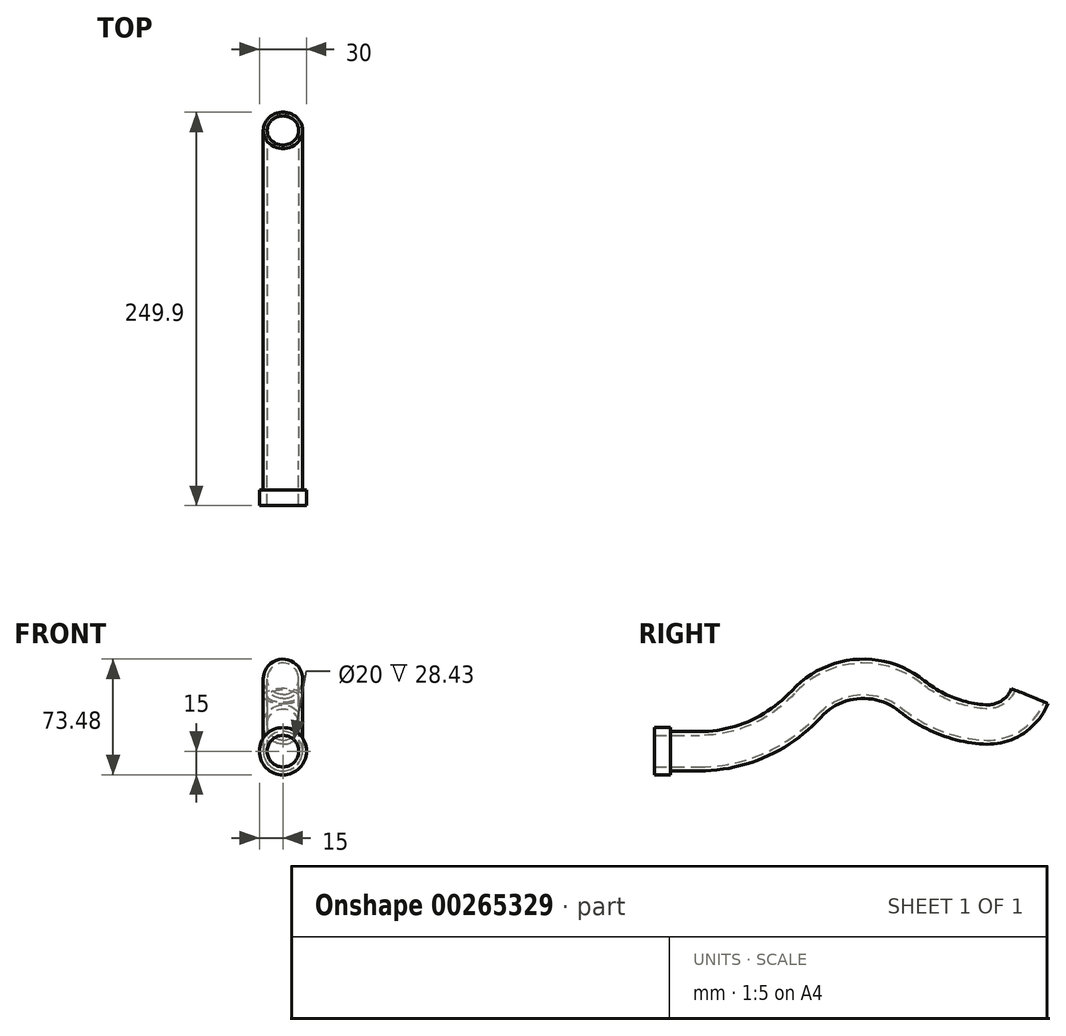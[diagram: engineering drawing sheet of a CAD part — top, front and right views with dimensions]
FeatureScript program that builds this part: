
annotation { "Feature Type Name" : "Feature", "Feature Type Description" : "" }
export const myFeature = defineFeature(function(context is Context, id is Id, definition is map)
    precondition{}
    {
        {
            var Q0;
            Q0=qCreatedBy(makeId("Front.planeOp"),FACE);
            var sketch = newSketch(context, id + "F0", { "sketchPlane" : qUnion([Q0])});
            skCircle(sketch, "E0", {"center": v(0, 0) * mm, "radius": 12.5 * mm});
            skCircle(sketch, "E1", {"center": v(0, 0) * mm, "radius": 10 * mm});
            skSolve(sketch);
        }
        {
            var Q0;
            Q0=qCreatedBy(makeId("Right.planeOp"),FACE);
            var sketch = newSketch(context, id + "F1", { "sketchPlane" : qUnion([Q0])});
            skLineSegment(sketch, "E2", {"start": v(0, 0) * mm, "end": v(28.43, 0) * mm});
            skArc(sketch, "E3", {"start": v(28.43, 0) * mm, "mid": v(65.58, 7.83) * mm, "end": v(96.4, 30) * mm});
            skArc(sketch, "E4", {"start": v(96.4, 30) * mm, "mid": v(128.96, 45.84) * mm, "end": v(163.51, 35) * mm});
            skArc(sketch, "E5", {"start": v(163.51, 35) * mm, "mid": v(185.2, 22.38) * mm, "end": v(209.72, 17) * mm});
            skArc(sketch, "E6", {"start": v(209.72, 17) * mm, "mid": v(226.91, 21.4) * mm, "end": v(238.32, 35) * mm});
            skSolve(sketch);
        }
        {
            var Q0;
            Q0 = qSketchRegion(id + "F0", true);
            var Q1;
            Q1=sQuery(id+"F1.wireOp",EDGE,"E2");
            var Q2;
            Q2=sQuery(id+"F1.wireOp",EDGE,"E3");
            var Q3;
            Q3=sQuery(id+"F1.wireOp",EDGE,"E4");
            var Q4;
            Q4=sQuery(id+"F1.wireOp",EDGE,"E5");
            var Q5;
            Q5=sQuery(id+"F1.wireOp",EDGE,"E6");
            sweep(context, id + "F2", {"profiles" : qUnion([Q0]), "path" : qUnion([Q1, Q2, Q3, Q4, Q5])});
        }
        {
            var Q0;
            Q0=qCreatedBy(makeId("Front.planeOp"),FACE);
            var sketch = newSketch(context, id + "F3", { "sketchPlane" : qUnion([Q0])});
            skCircle(sketch, "E7", {"center": v(0, 0) * mm, "radius": 15 * mm});
            skSolve(sketch);
        }
        {
            var Q0;
            Q0 = qSketchRegion(id + "F3", true);
            extrude(context, id + "F4", {"entities" : qUnion([Q0]), "operationType" : NewBodyOperationType.ADD, "oppositeDirection" : true, "depth" : 10 * mm});
        }
        {
            var Q0;
            Q0=makeQuery(id+"F4.boolean.opBoolean","MERGE",FACE,{"derivedFrom":[makeQuery(id+"F2.opSweep","CAP_FACE",FACE,{"disambiguationData":[OSD([sQuery(id+"F0.wireOp",EDGE,"E0"),sQuery(id+"F0.wireOp",EDGE,"E1"),sQuery(id+"F1.wireOp",VERTEX,"E2.start")])],"isStart":true}),makeQuery(id+"F4.opExtrude","CAP_FACE",FACE,{"disambiguationData":[OSD([sQuery(id+"F3.wireOp",EDGE,"E7")])],"isStart":true})]});
            var sketch = newSketch(context, id + "F5", { "sketchPlane" : qUnion([Q0])});
            skCircle(sketch, "E8", {"center": v(0, 0) * mm, "radius": 10 * mm});
            skSolve(sketch);
        }
        {
            var Q0;
            Q0 = qSketchRegion(id + "F5", true);
            extrude(context, id + "F6", {"entities" : qUnion([Q0]), "operationType" : NewBodyOperationType.REMOVE, "oppositeDirection" : true, "depth" : 10 * mm});
        }
    });
